# Revit family: Lighting_Fixture-Visa_Lighting-Voila_LED new
name_source: partatom
category: Lighting Fixtures
units: mm (PartAtom-declared; Revit-internal decimal feet)

## family parameters
Cut with Voids When Loaded = No
Host = Face
Light Source = Yes
OmniClass Number = 23.80.70.11
OmniClass Title = Luminaries for Internal Lighting
Part Type = Normal
Room Calculation Point = No
Round Connector Dimension = Use Diameter
Shared = No

## types (1)
- Not a Type - Load Type Catalog
    Apparent Load = 25 VA
    Assembly Code = D5020200
    C Depth = 0' - 5 27/32"
    C Diameter = 0' - 2"
    C Mud Frame Size = 0' - 0 1/2"
    C Radius = 0' - 1"
    Color Filter = 16777215
    Constraints = 1
    Control = 0
    Default Elevation = 0' - 0"
    Depth = 0' - 2 5/8"
    Description = Please Load Accompanying Type Catalog (.txt)
    Dimming Lamp Color Temperature Shift = <None>
    Frequency = 60 Hz
    Height = 0' - 2"
    Instruction Sheet Link = Please Load Accompanying Type Catalog (.txt)
    Junction Box Cover = No
    Keynote = 26 51 00
    Lamp = LED
    Lens = Diffuser - VISA - Matte White
    Manufacturer = Visa Lighting
    Model = Please Load Accompanying Type Catalog (.txt)
    Mud Frame = Yes
    Number of Lamps = 1
    Number of Poles = 1
    Phase = 1
    Photometric Web File = CV4167-L35K-L.ies
    Photometry Note = Please load ies file listed under Photometric Web File for accurate rendering.
    Power Factor = 1
    Product Documentation Link = Please Load Accompanying Type Catalog (.txt)
    Product Name = Voila Wall
    Product Page URL = https://www.visalighting.com
    Recessed Depth = 0' - 3 1/4"
    Tilt Angle = 180.00°
    URL = http://www.visalighting.com
    Version = 2020 – v1.0a
    Voltage = 120 V
    Voltage Comment = 120-277V, 50/60 Hz
    Warranty URL = https://www.visalighting.com
    Wattage Comments = 25 W
    Width = 1' - 11 1/2"

## geometry (parser evidence)
native form markers: Sweep x1
no freeform markers — native parametric forms only
